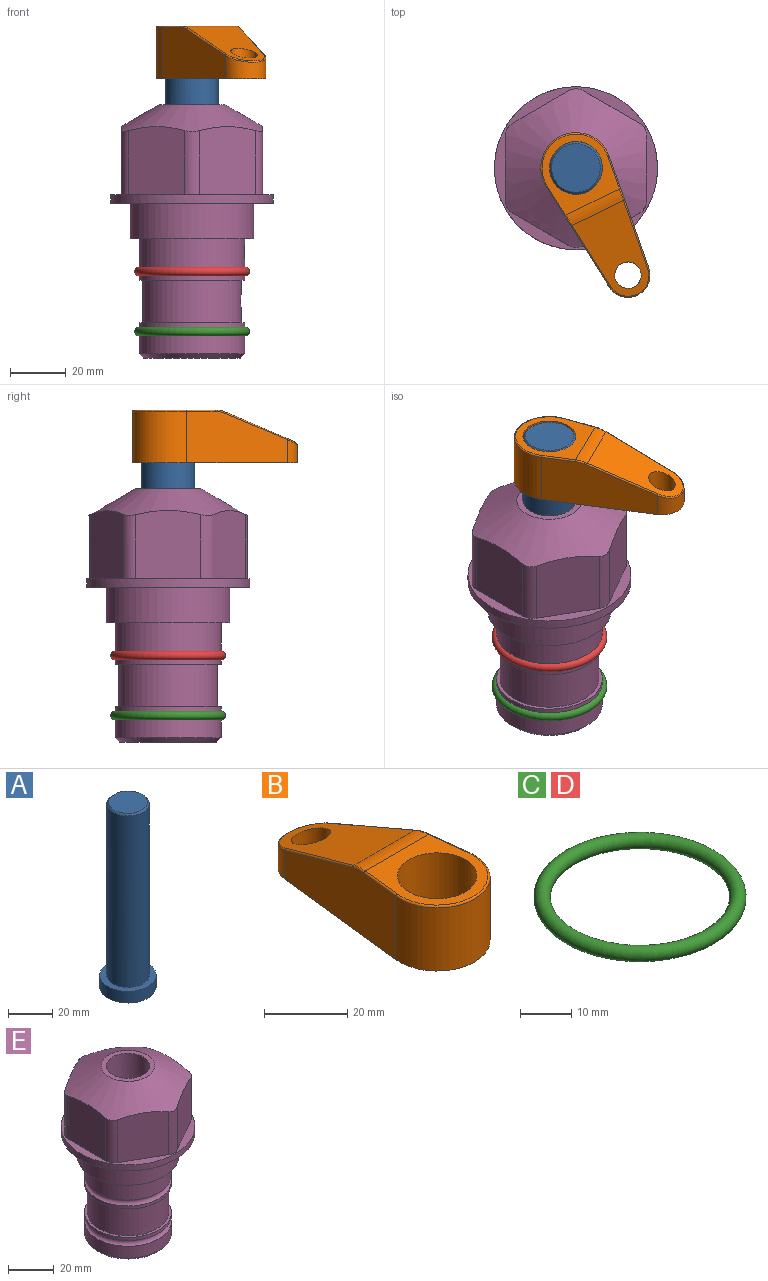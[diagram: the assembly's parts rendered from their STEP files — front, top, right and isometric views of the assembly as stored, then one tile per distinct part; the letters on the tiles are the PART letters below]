
ASSEMBLY  parts=5 mates=3
PART A: 6 faces, bbox 25.4x25.4x101.6 mm
  f0: plane 17.46x17.46mm, normal (0,0,1), area 239.5mm2, adj f5
  f1: plane 25.4x25.4mm, normal (0,0,-1), area 506.7mm2, adj f2
  f2: cylinder r=12.7mm len=25.4mm, axis (0,0,1), area 506.7mm2, adj f1,f3
  f3: plane 25.4x25.4mm, normal (0,0,1), area 221.7mm2, adj f2,f4
  f4: cylinder r=9.53mm len=94.46mm, axis (0,0,1), area 5653mm2, adj f3,f5
  f5: cone r=8.73mm half-angle=45deg, axis (0,0,-1), area 64.4mm2, adj f0,f4
PART B: 44 faces, bbox 27.5x64.5x19.1 mm
  f0: plane 2.3x0.95mm, normal (0,0,-1), area 1mm2, adj f25,f30,f34
  f1: plane 63.5x25.4mm, normal (0,0,-1), area 561.7mm2, adj f2,f3,f4,f5,f6,f7,f19,f20
  f2: cylinder r=12.7mm len=25.4mm, axis (0,0,-1), area 792.2mm2, adj f1,f3,f5,f13
  f3: plane 42.33x18.54mm, normal (0.99,0.11,0), area 647mm2, adj f1,f2,f4,f11,f12,f14
  f4: cylinder r=7.94mm len=15.78mm, axis (0,0,-1), area 158.6mm2, adj f1,f3,f5,f16
  f5: plane 42.33x18.54mm, normal (-0.99,0.11,0), area 647mm2, adj f1,f2,f4,f15,f17,f18
  f6: cylinder r=9.53mm len=19.05mm, axis (0,0,-1), area 1140.1mm2, adj f1,f8
  f7: cylinder r=4.76mm len=10.98mm, axis (0,0,-1), area 276.1mm2, adj f1,f9
  f8: plane 25.83x24.38mm, normal (0,0,1), area 262.2mm2, adj f6,f10,f11,f13,f15
  f9: plane 32.49x20.55mm, normal (0,0.34,0.94), area 489.9mm2, adj f7,f10,f14,f16,f18
  f10: cylinder r=12.7mm len=21.49mm, axis (-1,0,0), area 93.2mm2, adj f8,f9,f12,f17
  f11: cylinder r=0.51mm len=12.34mm, axis (0.11,-0.99,0), area 9.9mm2, adj f3,f8,f12,f13
  f12: bspline ~7.62x1.64mm, area 3.5mm2, adj f3,f10,f11,f14
  f13: torus R=12.19mm, axis (0,0,1), area 33.6mm2, adj f2,f8,f11,f15
  f14: cylinder r=0.51mm len=26.01mm, axis (0.1,-0.93,0.34), area 21.6mm2, adj f3,f9,f12,f16
  f15: cylinder r=0.51mm len=12.34mm, axis (0.11,0.99,0), area 9.9mm2, adj f5,f8,f13,f17
  f16: bspline ~15.78x7.05mm, area 15.7mm2, adj f4,f9,f14,f18
  f17: bspline ~7.62x1.64mm, area 3.5mm2, adj f5,f10,f15,f18
  f18: cylinder r=0.51mm len=26.01mm, axis (0.1,0.93,-0.34), area 21.6mm2, adj f5,f9,f16,f17
  f19: plane 21.6x14.29mm, normal (-0.99,-0.11,0), area 242.6mm2, adj f1,f26,f28,f34,f36,f38
  f20: plane 21.6x14.29mm, normal (0.99,-0.11,0), area 242.6mm2, adj f1,f27,f29,f37,f39,f41
  f21: cylinder r=12.7mm len=14.29mm, axis (0,0,-1), area 173.2mm2, adj f1,f26,f27,f30,f31,f33
  f22: cylinder r=7.94mm len=7.63mm, axis (0,0,-1), area 53.8mm2, adj f1,f28,f29,f42
  f23: plane 2.3x0.95mm, normal (0,0,-1), area 1mm2, adj f25,f33,f37
  f24: plane 17.94x12.32mm, normal (0,-0.34,-0.94), area 191.2mm2, adj f25,f38,f41,f42
  f25: cylinder r=9.53mm len=12.93mm, axis (-1,0,0), area 37.5mm2, adj f0,f23,f24,f31,f36,f39
  f26: cylinder r=1.59mm len=14.29mm, axis (0,0,-1), area 49mm2, adj f1,f19,f21,f32
  f27: cylinder r=1.59mm len=14.29mm, axis (0,0,-1), area 49mm2, adj f1,f20,f21,f35
  f28: cylinder r=1.59mm len=7.28mm, axis (0,0,-1), area 22.1mm2, adj f1,f19,f22,f40
  f29: cylinder r=1.59mm len=7.28mm, axis (0,0,-1), area 22.1mm2, adj f1,f20,f22,f43
  f30: torus R=14.29mm, axis (0,0,1), area 5.8mm2, adj f0,f21,f31,f32
  f31: bspline ~11.06x2.73mm, area 20.8mm2, adj f21,f25,f30,f33
  f32: sphere r=1.59mm, area 5.4mm2, adj f26,f30,f34
  f33: torus R=14.29mm, axis (0,0,1), area 5.8mm2, adj f21,f23,f31,f35
  f34: cylinder r=1.59mm len=1.68mm, axis (-0.11,0.99,0), area 2.4mm2, adj f0,f19,f32,f36
  f35: sphere r=1.59mm, area 5.4mm2, adj f27,f33,f37
  f36: bspline ~5.82x2.33mm, area 7.7mm2, adj f19,f25,f34,f38
  f37: cylinder r=1.59mm len=1.68mm, axis (0.11,0.99,0), area 2.4mm2, adj f20,f23,f35,f39
  f38: cylinder r=1.59mm len=18.33mm, axis (0.1,-0.93,0.34), area 46.7mm2, adj f19,f24,f36,f40
  f39: bspline ~5.82x2.33mm, area 7.7mm2, adj f20,f25,f37,f41
  f40: sphere r=1.59mm, area 3.6mm2, adj f28,f38,f42
  f41: cylinder r=1.59mm len=18.33mm, axis (0.1,0.93,-0.34), area 46.7mm2, adj f20,f24,f39,f43
  f42: bspline ~8.31x1.84mm, area 15.3mm2, adj f22,f24,f40,f43
  f43: sphere r=1.59mm, area 3.6mm2, adj f29,f41,f42
PART C: 1 faces, bbox 44.7x44.7x3.2 mm
  f0: torus R=19.05mm, axis (0,0,1), area 1193.9mm2
PART D: same geometry as C
PART E: 36 faces, bbox 58.7x58.7x91.2 mm
  f0: cylinder r=17.78mm len=35.56mm, axis (0,0,1), area 1670.8mm2, adj f23,f24,f31
  f1: cylinder r=19.05mm len=38.1mm, axis (0,0,1), area 1191.9mm2, adj f26,f27,f30
  f2: plane 58.66x58.66mm, normal (0,0,-1), area 1150.6mm2, adj f3,f28
  f3: cylinder r=29.33mm len=58.66mm, axis (0,0,-1), area 585.1mm2, adj f2,f4
  f4: plane 58.66x58.66mm, normal (0,0,1), area 475.9mm2, adj f3,f5,f6,f7,f8,f9,f10,f11
  f5: plane 24.5x20.32mm, normal (-0.5,0.87,0), area 562.8mm2, adj f4,f15,f16,f17
  f6: plane 24.5x20.32mm, normal (0.5,0.87,0), area 562.8mm2, adj f4,f14,f15,f17
  f7: plane 24.5x23.48mm, normal (1,0,0), area 562.8mm2, adj f4,f13,f14,f17
  f8: plane 24.5x20.32mm, normal (0.5,-0.87,0), area 562.8mm2, adj f4,f12,f13,f17
  f9: plane 24.5x20.32mm, normal (-0.5,-0.87,0), area 562.8mm2, adj f4,f11,f12,f17
  f10: plane 24.5x23.48mm, normal (-1,0,0), area 562.8mm2, adj f4,f11,f16,f17
  f11: cylinder r=5.08mm len=23.01mm, axis (0,0,-1), area 121.2mm2, adj f4,f9,f10,f17
  f12: cylinder r=5.08mm len=23.01mm, axis (0,0,-1), area 121.2mm2, adj f4,f8,f9,f17
  f13: cylinder r=5.08mm len=23.01mm, axis (0,0,-1), area 121.2mm2, adj f4,f7,f8,f17
  f14: cylinder r=5.08mm len=23.01mm, axis (0,0,-1), area 121.2mm2, adj f4,f6,f7,f17
  f15: cylinder r=5.08mm len=23.01mm, axis (0,0,-1), area 121.2mm2, adj f4,f5,f6,f17
  f16: cylinder r=5.08mm len=23.01mm, axis (0,0,-1), area 121.2mm2, adj f4,f5,f10,f17
  f17: cone r=11.73mm half-angle=60deg, axis (0,0,-1), area 2071.8mm2, adj f5,f6,f7,f8,f9,f10,f11,f12
  f18: plane 23.46x23.46mm, normal (0,0,1), area 147.4mm2, adj f17,f35
  f19: plane 34.93x34.93mm, normal (0,0,-1), area 958mm2, adj f29
  f20: cylinder r=19.05mm len=38.1mm, axis (0,0,1), area 760.1mm2, adj f21,f29
  f21: torus R=19.05mm, axis (0,0,1), area 565.3mm2, adj f20,f22
  f22: cylinder r=19.05mm len=38.1mm, axis (0,0,1), area 190mm2, adj f21,f23
  f23: plane 38.1x38.1mm, normal (0,0,1), area 146.9mm2, adj f0,f22
  f24: plane 38.1x38.1mm, normal (0,0,-1), area 146.9mm2, adj f0,f25
  f25: cylinder r=19.05mm len=38.1mm, axis (0,0,1), area 190mm2, adj f24,f26
  f26: torus R=19.05mm, axis (0,0,1), area 565.3mm2, adj f1,f25
  f27: plane 44.45x44.45mm, normal (0,0,-1), area 411.7mm2, adj f1,f28
  f28: cylinder r=22.23mm len=44.45mm, axis (0,0,1), area 1773.5mm2, adj f2,f27
  f29: cone r=19.05mm half-angle=45deg, axis (0,0,1), area 257.5mm2, adj f19,f20
  f30: cylinder r=3.17mm len=6.75mm, axis (-1,0,0), area 128mm2, adj f1,f33
  f31: cylinder r=3.17mm len=6.35mm, axis (-1,0,0), area 102.5mm2, adj f0,f33
  f32: plane 25.4x25.4mm, normal (0,0,1), area 506.7mm2, adj f33
  f33: cylinder r=12.7mm len=66.42mm, axis (0,0,-1), area 5236.2mm2, adj f30,f31,f32,f34
  f34: cone r=9.53mm half-angle=30deg, axis (0,0,-1), area 443.4mm2, adj f33,f35
  f35: cylinder r=9.53mm len=19.05mm, axis (0,0,-1), area 849mm2, adj f18,f34
PLACE A rot(axis=(0,0,-1),64.1deg) t=(0,0,-9.83)mm
PLACE B rot(axis=(0,0,-1),154.1deg) t=(0,0,44.78)mm
PLACE C t=(0,0,-21.59)mm
PLACE D at identity
PLACE E at identity fixed
MATE fastened C.f0 <-> E.f0  axis (0,0,1) through (0,0,-46.1)mm
MATE cylindrical A.f2 <-> E.f0  axis (0,0,1) through (0,0,15.8)mm
MATE fastened B.f2 <-> A.f2  axis (0,0,1) through (0,0,63.83)mm
